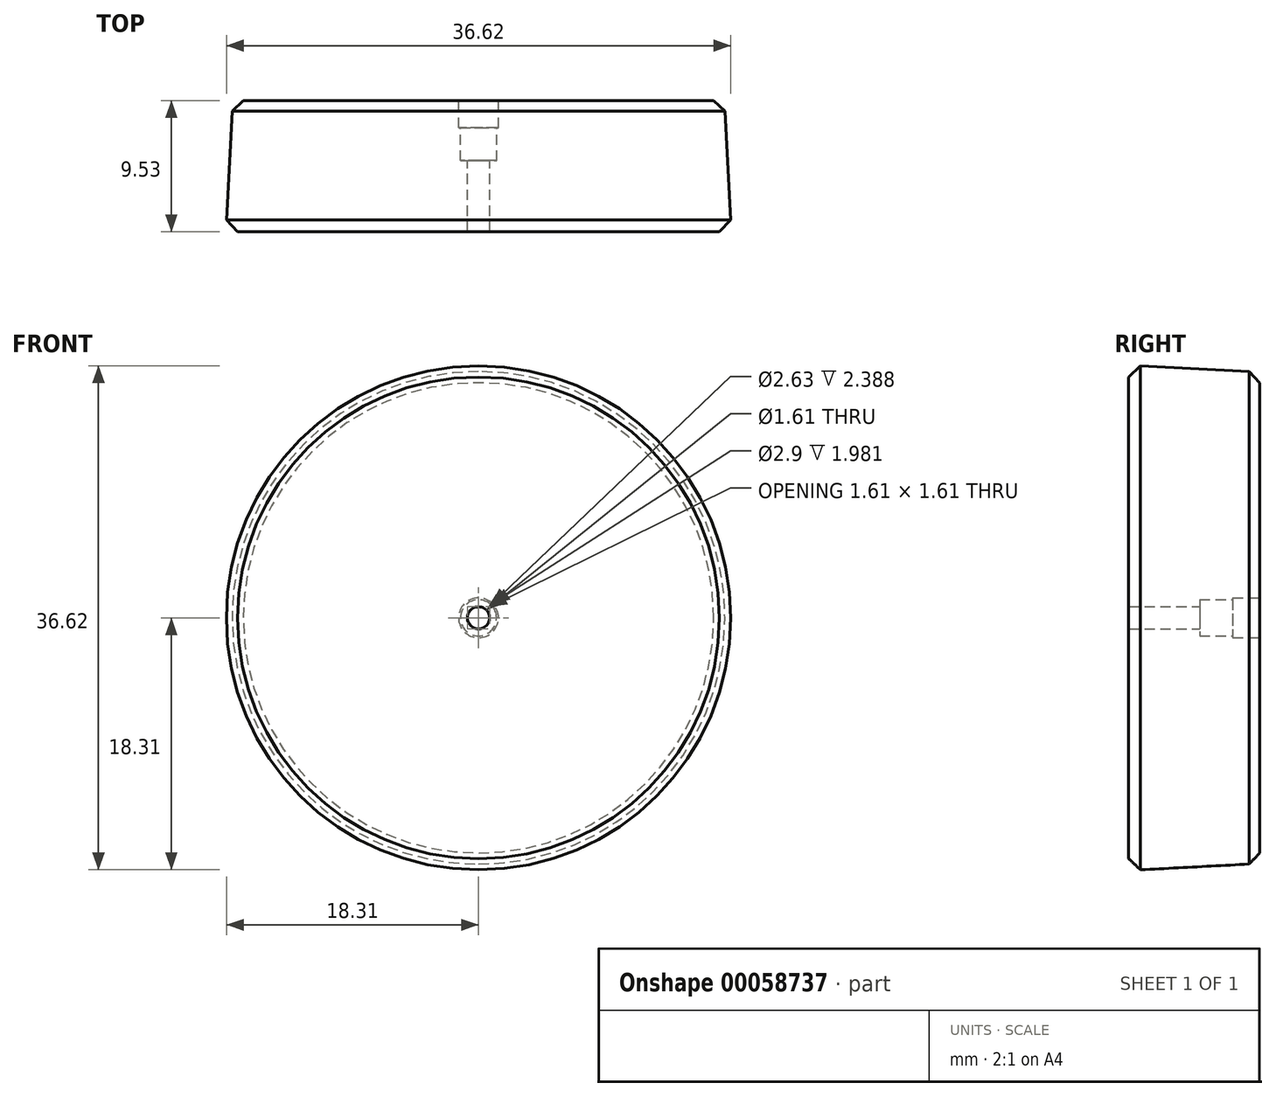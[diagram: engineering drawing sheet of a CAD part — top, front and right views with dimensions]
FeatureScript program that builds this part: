
annotation { "Feature Type Name" : "Feature", "Feature Type Description" : "" }
export const myFeature = defineFeature(function(context is Context, id is Id, definition is map)
    precondition{}
    {
        {
            var Q0;
            Q0=qCreatedBy(makeId("Front.planeOp"),FACE);
            var sketch = newSketch(context, id + "F0", { "sketchPlane" : qUnion([Q0])});
            skCircle(sketch, "E0", {"center": v(0, 0) * mm, "radius": 17.86 * mm});
            skSolve(sketch);
        }
        {
            var Q0;
            Q0 = qSketchRegion(id + "F0", true);
            extrude(context, id + "F1", {"entities" : qUnion([Q0]), "depth" : 9.52 * mm, "hasDraft" : true, "draftAngle" : 3 * degree});
        }
        {
            var Q0;
            Q0=sQuery(id+"F0.wireOp",VERTEX,"E0.center");
            var Q1;
            Q1=makeQuery(id+"F1.opExtrude","SWEPT_BODY",BODY,{"disambiguationData":[OSD([sQuery(id+"F0.wireOp",EDGE,"E0")])]});
            hole(context, id + "F2", {"style" : HoleStyle.SIMPLE, "holeDiameter" : 1.61 * mm, "endStyle" : HoleEndStyle.THROUGH, "oppositeDirection" : true, "locations" : qUnion([Q0]), "scope" : qUnion([Q1])});
        }
        {
            var Q0;
            Q0=sQuery(id+"F0.wireOp",VERTEX,"E0.center");
            var Q1;
            Q1=makeQuery(id+"F1.opExtrude","SWEPT_BODY",BODY,{"disambiguationData":[OSD([sQuery(id+"F0.wireOp",EDGE,"E0")])]});
            hole(context, id + "F3", {"style" : HoleStyle.C_BORE, "holeDiameter" : 1.61 * mm, "cBoreDiameter" : 2.63 * mm, "cBoreDepth" : 4.37 * mm, "endStyle" : HoleEndStyle.THROUGH, "oppositeDirection" : true, "locations" : qUnion([Q0]), "scope" : qUnion([Q1])});
        }
        {
            var Q0;
            Q0=sQuery(id+"F0.wireOp",VERTEX,"E0.center");
            var Q1;
            Q1=makeQuery(id+"F1.opExtrude","SWEPT_BODY",BODY,{"disambiguationData":[OSD([sQuery(id+"F0.wireOp",EDGE,"E0")])]});
            hole(context, id + "F4", {"style" : HoleStyle.C_BORE, "holeDiameter" : 1.63 * mm, "cBoreDiameter" : 2.9 * mm, "cBoreDepth" : 1.98 * mm, "endStyle" : HoleEndStyle.THROUGH, "oppositeDirection" : true, "locations" : qUnion([Q0]), "scope" : qUnion([Q1])});
        }
        {
            var Q0;
            Q0=makeQuery(id+"F1.opExtrude","CAP_EDGE",EDGE,{"disambiguationData":[OSD([sQuery(id+"F0.wireOp",EDGE,"E0")])],"isStart":true});
            chamfer(context, id + "F5", {"entities" : qUnion([Q0]), "width" : 0.81 * mm, "tangentPropagation" : true});
        }
        {
            var Q0;
            Q0=makeQuery(id+"F1.opExtrude","CAP_EDGE",EDGE,{"disambiguationData":[OSD([sQuery(id+"F0.wireOp",EDGE,"E0")])],"isStart":false});
            chamfer(context, id + "F6", {"entities" : qUnion([Q0]), "width" : 0.81 * mm, "tangentPropagation" : true});
        }
    });
